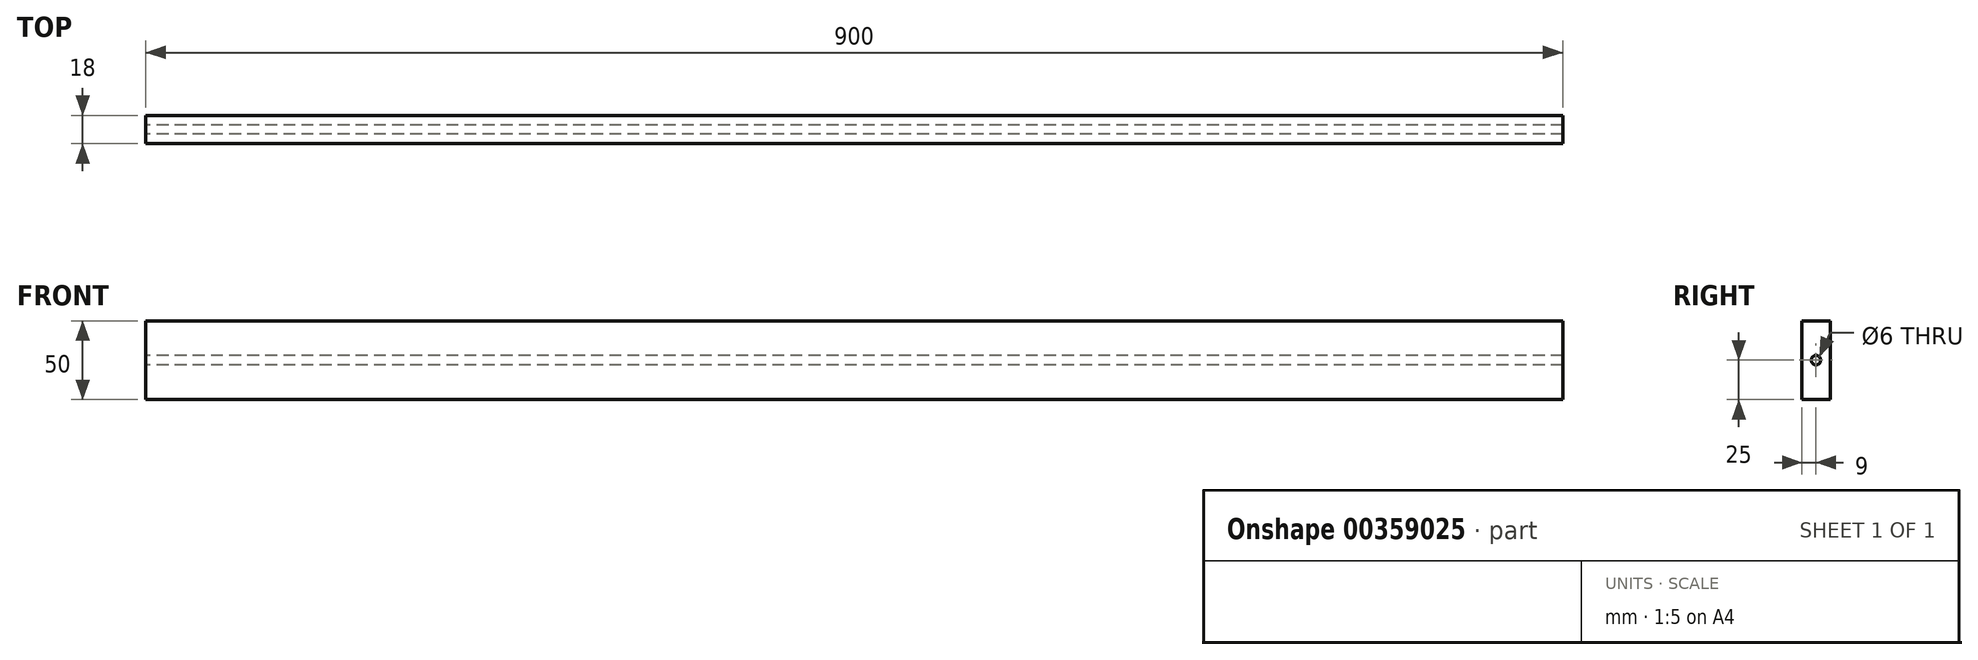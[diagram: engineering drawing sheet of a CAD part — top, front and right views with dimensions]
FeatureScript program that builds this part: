
annotation { "Feature Type Name" : "Feature", "Feature Type Description" : "" }
export const myFeature = defineFeature(function(context is Context, id is Id, definition is map)
    precondition{}
    {
        {
            var Q0;
            Q0=qCreatedBy(makeId("Front.planeOp"),FACE);
            var sketch = newSketch(context, id + "F0", { "sketchPlane" : qUnion([Q0])});
            skLineSegment(sketch, "E0.bottom", {"start": v(0, 0) * mm, "end": v(900, 0) * mm});
            skLineSegment(sketch, "E0.top", {"start": v(0, 50) * mm, "end": v(900, 50) * mm});
            skLineSegment(sketch, "E0.left", {"start": v(0, 0) * mm, "end": v(0, 50) * mm});
            skLineSegment(sketch, "E0.right", {"start": v(900, 0) * mm, "end": v(900, 50) * mm});
            skSolve(sketch);
        }
        {
            var Q0;
            Q0=makeQuery(id+"F0.imprint","IMPRINT",FACE,{"disambiguationData":[TD([[makeQuery(id+"F0.imprint","IMPRINT",EDGE,{"derivedFrom":sQuery(id+"F0.wireOp",EDGE,"E0.bottom")}),1.0]])]});
            extrude(context, id + "F1", {"entities" : qUnion([Q0]), "depth" : 18 * mm});
        }
        {
            var Q0;
            Q0=makeQuery(id+"F1.opExtrude","SWEPT_FACE",FACE,{"disambiguationData":[OSD([sQuery(id+"F0.wireOp",EDGE,"E0.left")])]});
            var sketch = newSketch(context, id + "F2", { "sketchPlane" : qUnion([Q0])});
            skLineSegment(sketch, "E1", {"start": v(9, 0) * mm, "end": v(9, 50) * mm, "construction": true});
            skCircle(sketch, "E2", {"center": v(9, 25) * mm, "radius": 3 * mm});
            skSolve(sketch);
        }
        {
            var Q0;
            Q0=makeQuery(id+"F2.imprint","IMPRINT",FACE,{"disambiguationData":[TD([[makeQuery(id+"F2.imprint","IMPRINT",EDGE,{"derivedFrom":sQuery(id+"F2.wireOp",EDGE,"E2")}),1.0]])]});
            extrude(context, id + "F3", {"entities" : qUnion([Q0]), "operationType" : NewBodyOperationType.REMOVE, "oppositeDirection" : true, "depth" : 25 * mm});
        }
        {
            var Q0;
            Q0 = qSketchRegion(id + "F2", true);
            extrude(context, id + "F4", {"entities" : qUnion([Q0]), "operationType" : NewBodyOperationType.REMOVE, "endBound" : BoundingType.THROUGH_ALL, "oppositeDirection" : true, "depth" : 246 * mm, "hasSecondDirection" : true, "secondDirectionOppositeDirection" : false, "secondDirectionDepth" : 25 * mm});
        }
    });
